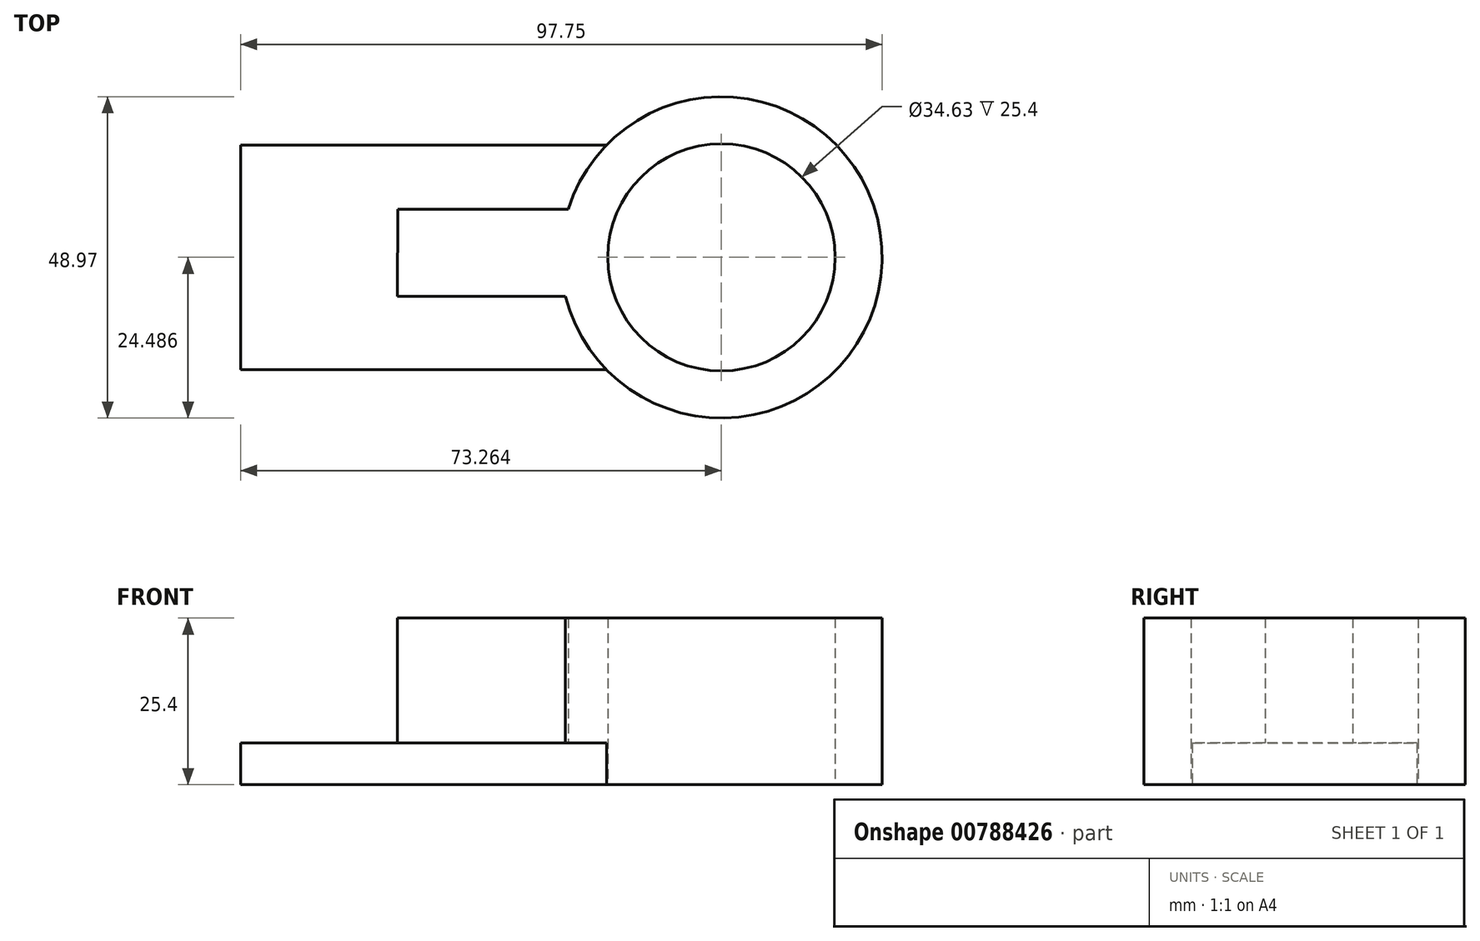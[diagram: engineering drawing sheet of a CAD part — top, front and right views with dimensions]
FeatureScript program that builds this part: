
annotation { "Feature Type Name" : "Feature", "Feature Type Description" : "" }
export const myFeature = defineFeature(function(context is Context, id is Id, definition is map)
    precondition{}
    {
        {
            var Q0;
            Q0=qCreatedBy(makeId("Top.planeOp"),FACE);
            var sketch = newSketch(context, id + "F0", { "sketchPlane" : qUnion([Q0])});
            skLineSegment(sketch, "E0.right", {"start": v(-28.56, -5.9) * mm, "end": v(-28.56, 28.32) * mm});
            skPoint(sketch, "E0.middle", {"position": v(8.07, 11.2) * mm});
            skArc(sketch, "E1", {"start": v(44.7, 28.32) * mm, "mid": v(27.6, 11.2) * mm, "end": v(44.7, -5.9) * mm});
            skCircle(sketch, "E2", {"center": v(44.7, 11.2) * mm, "radius": 17.31 * mm});
            skCircle(sketch, "E3", {"center": v(44.7, 11.2) * mm, "radius": 24.49 * mm});
            skLineSegment(sketch, "E4", {"start": v(-28.56, 28.32) * mm, "end": v(27.19, 28.32) * mm});
            skLineSegment(sketch, "E5", {"start": v(-28.56, -5.9) * mm, "end": v(27.19, -5.9) * mm});
            skLineSegment(sketch, "E6", {"start": v(20.96, 5.23) * mm, "end": v(-4.68, 5.23) * mm});
            skLineSegment(sketch, "E7", {"start": v(21.34, 18.54) * mm, "end": v(-4.58, 18.54) * mm});
            skLineSegment(sketch, "E8", {"start": v(-4.58, 18.54) * mm, "end": v(-4.68, 5.23) * mm});
            skSolve(sketch);
        }
        {
            var Q0;
            Q0=makeQuery(id+"F0.imprint","IMPRINT",FACE,{"disambiguationData":[TD([[makeQuery(id+"F0.imprint","IMPRINT",EDGE,{"derivedFrom":sQuery(id+"F0.wireOp",EDGE,"E0.right")}),-1.0]])]});
            extrude(context, id + "F1", {"entities" : qUnion([Q0]), "depth" : 6.35 * mm, "offsetDistance" : 25.4 * mm});
        }
        {
            var Q0;
            Q0=makeQuery(id+"F0.imprint","IMPRINT",FACE,{"disambiguationData":[TD([[makeQuery(id+"F0.imprint","IMPRINT",EDGE,{"derivedFrom":sQuery(id+"F0.wireOp",EDGE,"E2")}),-1.0]])]});
            extrude(context, id + "F2", {"entities" : qUnion([Q0]), "operationType" : NewBodyOperationType.ADD, "depth" : 25.4 * mm, "offsetDistance" : 25.4 * mm});
        }
        {
            var Q0;
            {var subQ0=sQuery(id+"F0.wireOp",EDGE,"E6");Q0=makeQuery(id+"F0.imprint","IMPRINT",FACE,{"disambiguationData":[TD([[makeQuery(id+"F0.imprint","IMPRINT",EDGE,{"derivedFrom":subQ0}),-1.0]])]});}
            extrude(context, id + "F3", {"entities" : qUnion([Q0]), "operationType" : NewBodyOperationType.ADD, "depth" : 25.4 * mm, "offsetDistance" : 25.4 * mm});
        }
    });
